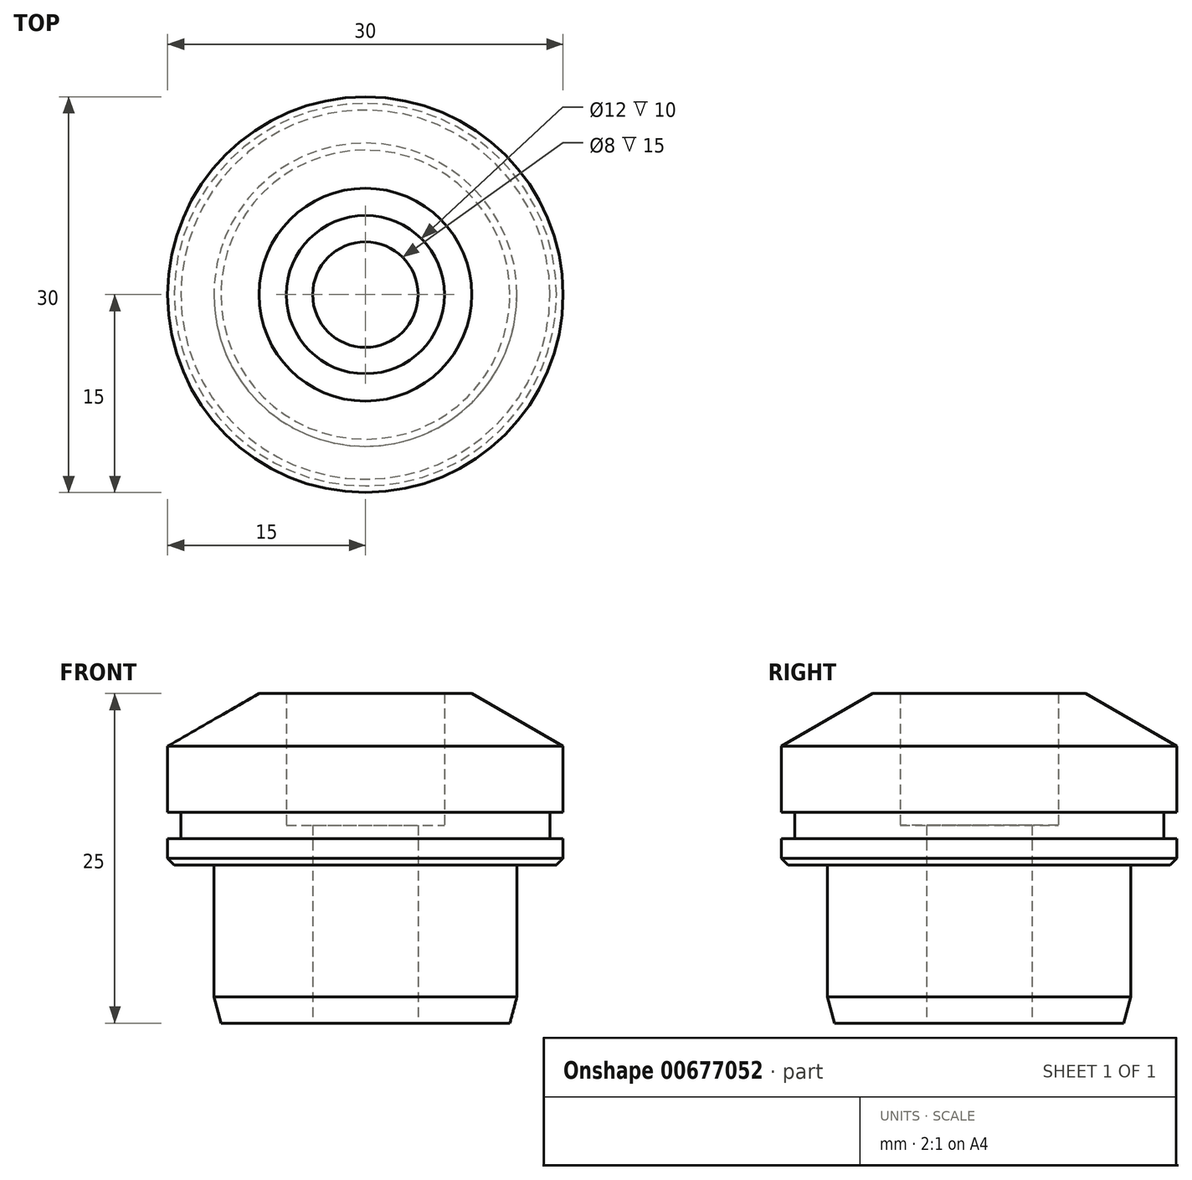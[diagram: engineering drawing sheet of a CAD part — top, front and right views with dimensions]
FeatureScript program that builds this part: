
annotation { "Feature Type Name" : "Feature", "Feature Type Description" : "" }
export const myFeature = defineFeature(function(context is Context, id is Id, definition is map)
    precondition{}
    {
        {
            var Q0;
            Q0=qCreatedBy(makeId("Front.planeOp"),FACE);
            var sketch = newSketch(context, id + "F0", { "sketchPlane" : qUnion([Q0])});
            skLineSegment(sketch, "E0", {"start": v(-6, 25) * mm, "end": v(-8.07, 25) * mm});
            skLineSegment(sketch, "E1", {"start": v(-15, 21) * mm, "end": v(-15, 16) * mm});
            skLineSegment(sketch, "E2", {"start": v(-15, 12) * mm, "end": v(-11.5, 12) * mm});
            skLineSegment(sketch, "E3", {"start": v(-11.5, 12) * mm, "end": v(-11.5, 0) * mm});
            skLineSegment(sketch, "E4", {"start": v(-11.5, 0) * mm, "end": v(-4, 0) * mm});
            skLineSegment(sketch, "E5", {"start": v(-8.07, 25) * mm, "end": v(-15, 21) * mm});
            skLineSegment(sketch, "E6", {"start": v(-6, 25) * mm, "end": v(-6, 15) * mm});
            skLineSegment(sketch, "E7", {"start": v(-6, 15) * mm, "end": v(-4, 15) * mm});
            skLineSegment(sketch, "E8", {"start": v(-4, 15) * mm, "end": v(-4, 0) * mm});
            skPoint(sketch, "E9.start.orphan", {"position": v(0, 36.85) * mm});
            skLineSegment(sketch, "E10", {"start": v(0, 0) * mm, "end": v(0, 30.22) * mm, "construction": true});
            skLineSegment(sketch, "E11", {"start": v(-15, 16) * mm, "end": v(-14, 16) * mm});
            skLineSegment(sketch, "E12", {"start": v(-14, 16) * mm, "end": v(-14, 14) * mm});
            skLineSegment(sketch, "E13", {"start": v(-14, 14) * mm, "end": v(-15, 14) * mm});
            skLineSegment(sketch, "E14.trimOffspring", {"start": v(-15, 14) * mm, "end": v(-15, 12) * mm});
            skSolve(sketch);
        }
        {
            var Q0;
            Q0 = qSketchRegion(id + "F0", true);
            var Q1;
            Q1=sQuery(id+"F0.wireOp",EDGE,"E10");
            revolve(context, id + "F1", {"entities" : qUnion([Q0]), "axis" : qUnion([Q1]), "revolveType" : RevolveType.FULL});
        }
        {
            var Q0;
            Q0=makeQuery(id+"F1.opRevolve","SWEPT_EDGE",EDGE,{"disambiguationData":[OSD([sQuery(id+"F0.wireOp",EDGE,"E3"),sQuery(id+"F0.wireOp",EDGE,"E4")])]});
            chamfer(context, id + "F2", {"entities" : qUnion([Q0]), "chamferType" : ChamferType.OFFSET_ANGLE, "width" : 2 * mm, "oppositeDirection" : true, "angle" : 15 * degree, "tangentPropagation" : true});
        }
        {
            var Q0;
            Q0=makeQuery(id+"F1.opRevolve","SWEPT_EDGE",EDGE,{"disambiguationData":[OSD([sQuery(id+"F0.wireOp",EDGE,"E2"),sQuery(id+"F0.wireOp",EDGE,"E14.trimOffspring")])]});
            chamfer(context, id + "F3", {"entities" : qUnion([Q0]), "width" : .5 * mm, "tangentPropagation" : true});
        }
        {
            var Q0;
            Q0=qCreatedBy(makeId("Top.planeOp"),FACE);
            cPlane(context, id + "F4", {"entities" : qUnion([Q0]), "cplaneType" : CPlaneType.OFFSET, "offset" : 16 * mm, "width" : 150 * mm, "height" : 150 * mm});
        }
    });
